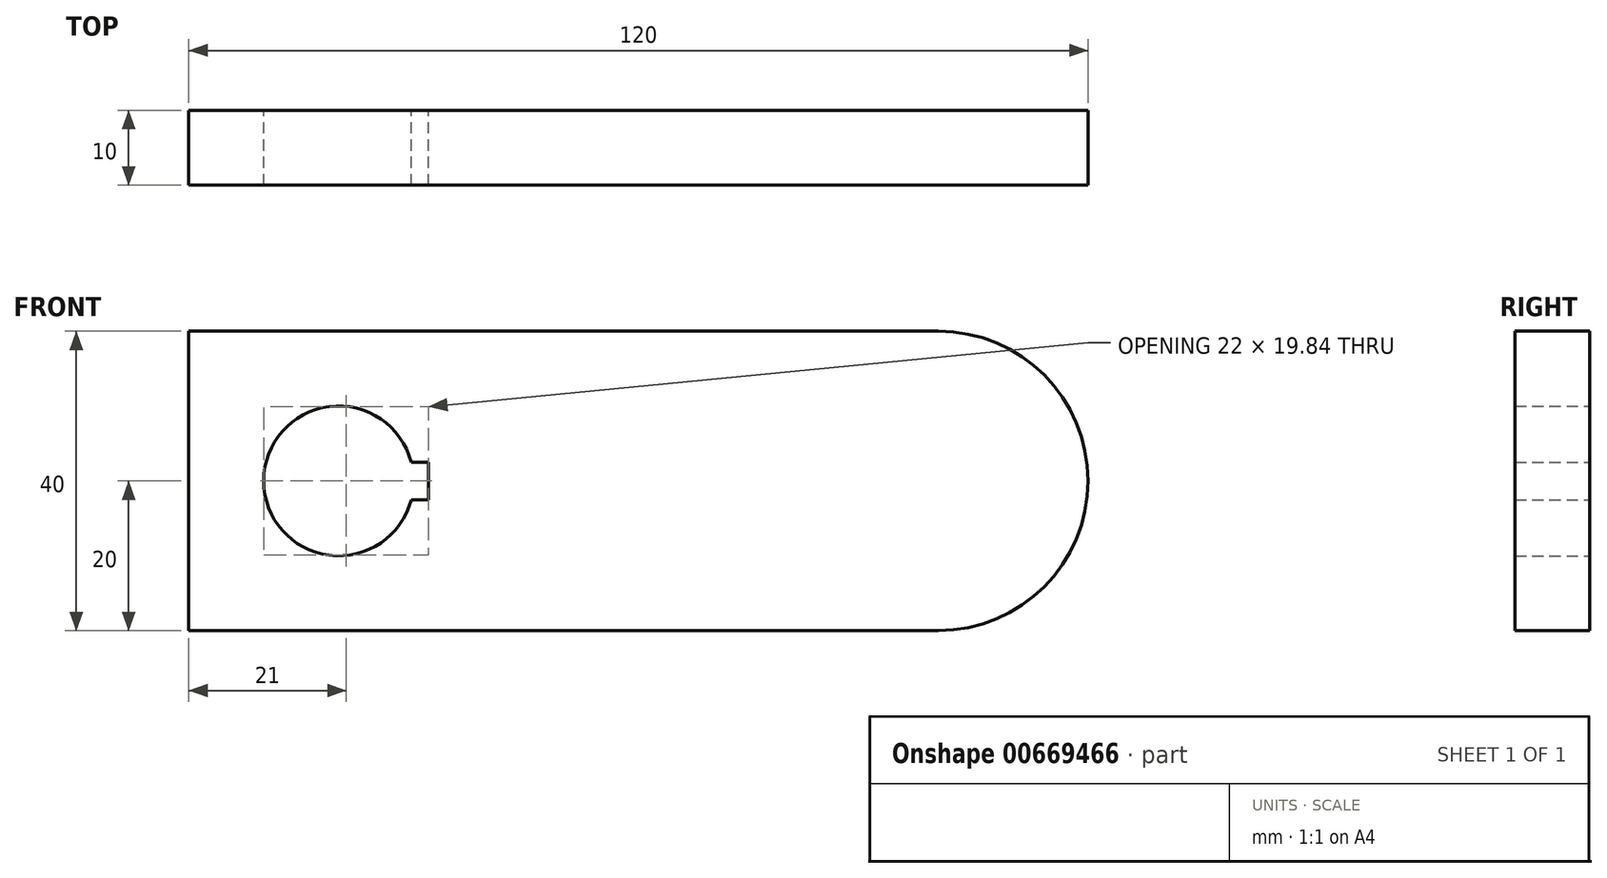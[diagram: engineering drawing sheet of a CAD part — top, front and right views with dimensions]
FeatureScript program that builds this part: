
annotation { "Feature Type Name" : "Feature", "Feature Type Description" : "" }
export const myFeature = defineFeature(function(context is Context, id is Id, definition is map)
    precondition{}
    {
        {
            var Q0;
            Q0=qCreatedBy(makeId("Front.planeOp"),FACE);
            var sketch = newSketch(context, id + "F0", { "sketchPlane" : qUnion([Q0])});
            skCircle(sketch, "E0", {"center": v(0, 0) * mm, "radius": 10 * mm});
            skLineSegment(sketch, "E1", {"start": v(-20, 0) * mm, "end": v(-20, -20) * mm});
            skLineSegment(sketch, "E2", {"start": v(-20, -20) * mm, "end": v(80, -20) * mm});
            skLineSegment(sketch, "E3", {"start": v(80, 20) * mm, "end": v(-20, 20) * mm});
            skLineSegment(sketch, "E4", {"start": v(-20, 20) * mm, "end": v(-20, 0) * mm});
            skLineSegment(sketch, "E5", {"start": v(12, 0) * mm, "end": v(12, 2.5) * mm});
            skLineSegment(sketch, "E6", {"start": v(12, 0) * mm, "end": v(12, -2.5) * mm});
            skLineSegment(sketch, "E7", {"start": v(12, -2.5) * mm, "end": v(9.68, -2.5) * mm});
            skLineSegment(sketch, "E8", {"start": v(12, 2.5) * mm, "end": v(9.68, 2.5) * mm});
            skArc(sketch, "E9", {"start": v(80, -20) * mm, "mid": v(100, 0) * mm, "end": v(80, 20) * mm});
            skSolve(sketch);
        }
        {
            var Q0;
            Q0=makeQuery(id+"F0.imprint","IMPRINT",FACE,{"disambiguationData":[TD([[makeQuery(id+"F0.imprint","IMPRINT",EDGE,{"derivedFrom":sQuery(id+"F0.wireOp",EDGE,"E1")}),1.0]])]});
            extrude(context, id + "F1", {"entities" : qUnion([Q0]), "depth" : 10 * mm, "offsetDistance" : 25 * mm});
        }
    });
